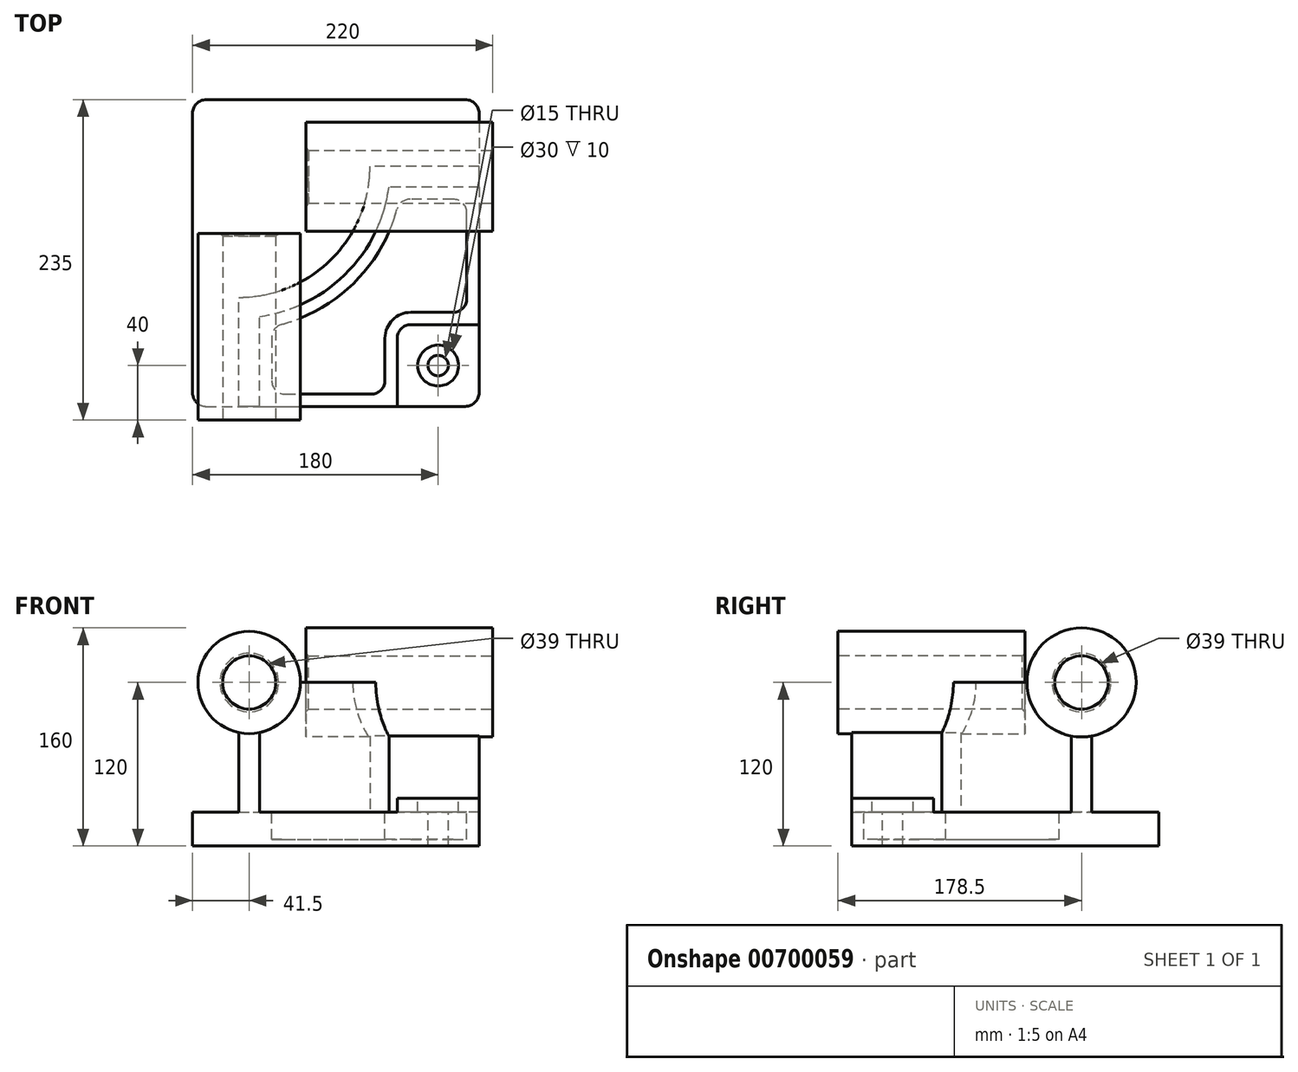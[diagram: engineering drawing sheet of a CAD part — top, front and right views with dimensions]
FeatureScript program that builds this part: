
annotation { "Feature Type Name" : "Feature", "Feature Type Description" : "" }
export const myFeature = defineFeature(function(context is Context, id is Id, definition is map)
    precondition{}
    {
        {
            var Q0;
            Q0=qCreatedBy(makeId("Top.planeOp"),FACE);
            var sketch = newSketch(context, id + "F0", { "sketchPlane" : qUnion([Q0])});
            skLineSegment(sketch, "E0.bottom", {"start": v(-105, 112.5) * mm, "end": v(105, 112.5) * mm});
            skLineSegment(sketch, "E0.top", {"start": v(-105, -112.5) * mm, "end": v(105, -112.5) * mm});
            skLineSegment(sketch, "E0.left", {"start": v(-105, 112.5) * mm, "end": v(-105, -112.5) * mm});
            skLineSegment(sketch, "E0.right", {"start": v(105, 112.5) * mm, "end": v(105, -112.5) * mm});
            skPoint(sketch, "E0.middle", {"position": v(0, 0) * mm});
            skSolve(sketch);
        }
        {
            var Q0;
            Q0=makeQuery(id+"F0.imprint","IMPRINT",FACE,{"disambiguationData":[TD([[makeQuery(id+"F0.imprint","IMPRINT",EDGE,{"derivedFrom":sQuery(id+"F0.wireOp",EDGE,"E0.bottom")}),-1.0]])]});
            extrude(context, id + "F1", {"entities" : qUnion([Q0]), "depth" : 25 * mm, "offsetDistance" : 25 * mm});
        }
        {
            var Q0;
            Q0=makeQuery(id+"F1.opExtrude","CAP_FACE",FACE,{"disambiguationData":[OSD([sQuery(id+"F0.wireOp",EDGE,"E0.bottom"),sQuery(id+"F0.wireOp",EDGE,"E0.top"),sQuery(id+"F0.wireOp",EDGE,"E0.left"),sQuery(id+"F0.wireOp",EDGE,"E0.right")])],"isStart":false});
            var sketch = newSketch(context, id + "F2", { "sketchPlane" : qUnion([Q0])});
            skLineSegment(sketch, "E1", {"start": v(105, 63.5) * mm, "end": v(25, 63.5) * mm});
            skLineSegment(sketch, "E2", {"start": v(-71, -112.5) * mm, "end": v(-71, -32.5) * mm});
            skArc(sketch, "E3", {"start": v(-71, -32.5) * mm, "mid": v(-3.12, -4.38) * mm, "end": v(25, 63.5) * mm});
            skLineSegment(sketch, "E4", {"start": v(-71, 63.5) * mm, "end": v(25, 63.5) * mm, "construction": true});
            skLineSegment(sketch, "E5", {"start": v(-71, 63.5) * mm, "end": v(-71, -32.5) * mm, "construction": true});
            skLineSegment(sketch, "E6.0", {"start": v(105, 48.5) * mm, "end": v(38.98, 48.5) * mm});
            skArc(sketch, "E6.1", {"start": v(-56, -46.48) * mm, "mid": v(7.49, -14.99) * mm, "end": v(38.98, 48.5) * mm});
            skLineSegment(sketch, "E6.2", {"start": v(-56, -112.5) * mm, "end": v(-56, -46.48) * mm});
            skLineSegment(sketch, "E7.0", {"start": v(105, 112.5) * mm, "end": v(105, -112.5) * mm});
            skLineSegment(sketch, "E7.1", {"start": v(-105, -112.5) * mm, "end": v(105, -112.5) * mm});
            skSolve(sketch);
        }
        {
            var Q0;
            {var subQ2=sQuery(id+"F2.wireOp",EDGE,"E1");Q0=makeQuery(id+"F2.imprint","IMPRINT",FACE,{"disambiguationData":[TD([[makeQuery(id+"F2.imprint","IMPRINT",EDGE,{"derivedFrom":subQ2}),1.0]])]});}
            extrude(context, id + "F3", {"entities" : qUnion([Q0]), "operationType" : NewBodyOperationType.ADD, "depth" : 95 * mm, "offsetDistance" : 25 * mm});
        }
        {
            var Q0;
            Q0=makeQuery(id+"F3.boolean.opBoolean","MERGE",FACE,{"derivedFrom":[makeQuery(id+"F1.opExtrude","SWEPT_FACE",FACE,{"disambiguationData":[OSD([sQuery(id+"F0.wireOp",EDGE,"E0.top")])]}),makeQuery(id+"F3.opExtrude","SWEPT_FACE",FACE,{"disambiguationData":[OSD([sQuery(id+"F2.wireOp",EDGE,"E7.1")])]})]});
            var sketch = newSketch(context, id + "F4", { "sketchPlane" : qUnion([Q0])});
            skCircle(sketch, "E8", {"center": v(-63.5, 120) * mm, "radius": 37.5 * mm});
            skSolve(sketch);
        }
        {
            var Q0;
            Q0 = qSketchRegion(id + "F4", true);
            extrude(context, id + "F5", {"entities" : qUnion([Q0]), "operationType" : NewBodyOperationType.ADD, "depth" : 10 * mm, "offsetDistance" : 25 * mm, "hasSecondDirection" : true, "secondDirectionOppositeDirection" : true, "secondDirectionDepth" : (137 - 10) * mm});
        }
        {
            var Q0;
            Q0=makeQuery(id+"F3.boolean.opBoolean","MERGE",FACE,{"derivedFrom":[makeQuery(id+"F1.opExtrude","SWEPT_FACE",FACE,{"disambiguationData":[OSD([sQuery(id+"F0.wireOp",EDGE,"E0.right")])]}),makeQuery(id+"F3.opExtrude","SWEPT_FACE",FACE,{"disambiguationData":[OSD([sQuery(id+"F2.wireOp",EDGE,"E7.0")])]})]});
            var sketch = newSketch(context, id + "F6", { "sketchPlane" : qUnion([Q0])});
            skCircle(sketch, "E9", {"center": v(56, 120) * mm, "radius": 40 * mm});
            skSolve(sketch);
        }
        {
            var Q0;
            Q0 = qSketchRegion(id + "F6", true);
            extrude(context, id + "F7", {"entities" : qUnion([Q0]), "operationType" : NewBodyOperationType.ADD, "depth" : 10 * mm, "offsetDistance" : 25 * mm, "hasSecondDirection" : true, "secondDirectionOppositeDirection" : true, "secondDirectionDepth" : (137 - 10) * mm});
        }
        {
            var Q0;
            {var subQ0=sQuery(id+"F0.wireOp",EDGE,"E0.right");var subQ1=sQuery(id+"F0.wireOp",EDGE,"E0.top");Q0=makeQuery(id+"F3.boolean.opBoolean","SPLIT",FACE,{"disambiguationData":[TD([makeQuery(id+"F3.opExtrude","SWEPT_FACE",FACE,{"disambiguationData":[OSD([sQuery(id+"F2.wireOp",EDGE,"E6.0")])]})])],"derivedFrom":makeQuery(id+"F1.opExtrude","CAP_FACE",FACE,{"disambiguationData":[OSD([sQuery(id+"F0.wireOp",EDGE,"E0.bottom"),subQ1,sQuery(id+"F0.wireOp",EDGE,"E0.left"),subQ0])],"isStart":false})});}
            var sketch = newSketch(context, id + "F8", { "sketchPlane" : qUnion([Q0])});
            skLineSegment(sketch, "E10.bottom", {"start": v(105, -112.5) * mm, "end": v(45, -112.5) * mm});
            skLineSegment(sketch, "E10.top", {"start": v(105, -52.5) * mm, "end": v(45, -52.5) * mm});
            skLineSegment(sketch, "E10.left", {"start": v(105, -112.5) * mm, "end": v(105, -52.5) * mm});
            skLineSegment(sketch, "E10.right", {"start": v(45, -112.5) * mm, "end": v(45, -52.5) * mm});
            skSolve(sketch);
        }
        {
            var Q0;
            Q0 = qSketchRegion(id + "F8", true);
            extrude(context, id + "F9", {"entities" : qUnion([Q0]), "operationType" : NewBodyOperationType.ADD, "depth" : 10 * mm, "offsetDistance" : 25 * mm});
        }
        {
            var Q0;
            Q0=makeQuery(id+"F9.opExtrude","SWEPT_EDGE",EDGE,{"disambiguationData":[OSD([sQuery(id+"F8.wireOp",EDGE,"E10.top"),sQuery(id+"F8.wireOp",EDGE,"E10.right")])]});
            fillet(context, id + "F10", {"entities" : qUnion([Q0]), "radius" : 10 * mm, "tangentPropagation" : true, "allowEdgeOverflow" : false});
        }
        {
            var Q0;
            {var subQ0=sQuery(id+"F0.wireOp",EDGE,"E0.right");var subQ1=sQuery(id+"F0.wireOp",EDGE,"E0.top");Q0=makeQuery(id+"F3.boolean.opBoolean","SPLIT",FACE,{"disambiguationData":[TD([makeQuery(id+"F3.opExtrude","SWEPT_FACE",FACE,{"disambiguationData":[OSD([sQuery(id+"F2.wireOp",EDGE,"E6.0")])]})])],"derivedFrom":makeQuery(id+"F1.opExtrude","CAP_FACE",FACE,{"disambiguationData":[OSD([sQuery(id+"F0.wireOp",EDGE,"E0.bottom"),subQ1,sQuery(id+"F0.wireOp",EDGE,"E0.left"),subQ0])],"isStart":false})});}
            var sketch = newSketch(context, id + "F11", { "sketchPlane" : qUnion([Q0])});
            skLineSegment(sketch, "E11.0", {"start": v(-47, -54.08) * mm, "end": v(-47, -103.5) * mm});
            skArc(sketch, "E11.1", {"start": v(46.58, 39.5) * mm, "mid": v(13.85, -21.35) * mm, "end": v(-47, -54.08) * mm});
            skLineSegment(sketch, "E11.2", {"start": v(-47, -103.5) * mm, "end": v(36, -103.5) * mm});
            skLineSegment(sketch, "E11.3", {"start": v(96, 39.5) * mm, "end": v(46.58, 39.5) * mm});
            skLineSegment(sketch, "E11.4", {"start": v(36, -103.5) * mm, "end": v(36, -62.5) * mm});
            skArc(sketch, "E11.5", {"start": v(36, -62.5) * mm, "mid": v(41.56, -49.06) * mm, "end": v(55, -43.5) * mm});
            skLineSegment(sketch, "E11.6", {"start": v(55, -43.5) * mm, "end": v(96, -43.5) * mm});
            skLineSegment(sketch, "E11.7", {"start": v(96, -43.5) * mm, "end": v(96, 39.5) * mm});
            skSolve(sketch);
        }
        {
            var Q0;
            Q0 = qSketchRegion(id + "F11", true);
            extrude(context, id + "F12", {"entities" : qUnion([Q0]), "operationType" : NewBodyOperationType.REMOVE, "oppositeDirection" : true, "depth" : 20 * mm, "offsetDistance" : 25 * mm});
        }
        {
            var Q0;
            Q0=makeQuery(id+"F9.opExtrude","CAP_FACE",FACE,{"disambiguationData":[OSD([sQuery(id+"F8.wireOp",EDGE,"E10.bottom"),sQuery(id+"F8.wireOp",EDGE,"E10.top"),sQuery(id+"F8.wireOp",EDGE,"E10.left"),sQuery(id+"F8.wireOp",EDGE,"E10.right")])],"isStart":false});
            var sketch = newSketch(context, id + "F13", { "sketchPlane" : qUnion([Q0])});
            skCircle(sketch, "E12", {"center": v(75, -82.5) * mm, "radius": 15 * mm});
            skSolve(sketch);
        }
        {
            var Q0;
            Q0=sQuery(id+"F13.wireOp",VERTEX,"E12.center");
            var Q1;
            Q1=makeQuery(id+"F1.opExtrude","SWEPT_BODY",BODY,{"disambiguationData":[OSD([sQuery(id+"F0.wireOp",EDGE,"E0.bottom"),sQuery(id+"F0.wireOp",EDGE,"E0.top"),sQuery(id+"F0.wireOp",EDGE,"E0.left"),sQuery(id+"F0.wireOp",EDGE,"E0.right")])]});
            hole(context, id + "F14", {"style" : HoleStyle.C_BORE, "endStyle" : HoleEndStyle.THROUGH, "holeDiameter" : 15 * mm, "cBoreDiameter" : 30 * mm, "cBoreDepth" : 10 * mm, "majorDiameter" : 5 * mm, "isTappedThrough" : true, "tappedDepth" : 12 * mm, "tapClearance" : 3, "locations" : qUnion([Q0]), "scope" : qUnion([Q1])});
        }
        {
            var Q0;
            Q0=makeQuery(id+"F12.boolean.opBoolean","COPY",EDGE,{"derivedFrom":makeQuery(id+"F12.opExtrude","SWEPT_EDGE",EDGE,{"disambiguationData":[OSD([sQuery(id+"F11.wireOp",EDGE,"E11.0"),sQuery(id+"F11.wireOp",EDGE,"E11.1")])]})});
            var Q1;
            Q1=makeQuery(id+"F12.boolean.opBoolean","COPY",EDGE,{"derivedFrom":makeQuery(id+"F12.opExtrude","SWEPT_EDGE",EDGE,{"disambiguationData":[OSD([sQuery(id+"F11.wireOp",EDGE,"E11.1"),sQuery(id+"F11.wireOp",EDGE,"E11.3")])]})});
            var Q2;
            Q2=makeQuery(id+"F12.boolean.opBoolean","COPY",EDGE,{"derivedFrom":makeQuery(id+"F12.opExtrude","SWEPT_EDGE",EDGE,{"disambiguationData":[OSD([sQuery(id+"F11.wireOp",EDGE,"E11.3"),sQuery(id+"F11.wireOp",EDGE,"E11.7")])]})});
            var Q3;
            Q3=makeQuery(id+"F12.boolean.opBoolean","COPY",EDGE,{"derivedFrom":makeQuery(id+"F12.opExtrude","SWEPT_EDGE",EDGE,{"disambiguationData":[OSD([sQuery(id+"F11.wireOp",EDGE,"E11.6"),sQuery(id+"F11.wireOp",EDGE,"E11.7")])]})});
            var Q4;
            Q4=makeQuery(id+"F12.boolean.opBoolean","COPY",EDGE,{"derivedFrom":makeQuery(id+"F12.opExtrude","SWEPT_EDGE",EDGE,{"disambiguationData":[OSD([sQuery(id+"F11.wireOp",EDGE,"E11.2"),sQuery(id+"F11.wireOp",EDGE,"E11.4")])]})});
            var Q5;
            Q5=makeQuery(id+"F12.boolean.opBoolean","COPY",EDGE,{"derivedFrom":makeQuery(id+"F12.opExtrude","SWEPT_EDGE",EDGE,{"disambiguationData":[OSD([sQuery(id+"F11.wireOp",EDGE,"E11.0"),sQuery(id+"F11.wireOp",EDGE,"E11.2")])]})});
            fillet(context, id + "F15", {"entities" : qUnion([Q0, Q1, Q2, Q3, Q4, Q5]), "radius" : 10 * mm, "tangentPropagation" : true, "allowEdgeOverflow" : false});
        }
        {
            var Q0;
            Q0=makeQuery(id+"F5.opExtrude","CAP_FACE",FACE,{"disambiguationData":[OSD([sQuery(id+"F4.wireOp",EDGE,"E8")])],"isStart":false});
            var sketch = newSketch(context, id + "F16", { "sketchPlane" : qUnion([Q0])});
            skCircle(sketch, "E13", {"center": v(-63.5, 120) * mm, "radius": 19.5 * mm});
            skSolve(sketch);
        }
        {
            var Q0;
            Q0 = qSketchRegion(id + "F16", true);
            extrude(context, id + "F17", {"entities" : qUnion([Q0]), "operationType" : NewBodyOperationType.REMOVE, "endBound" : BoundingType.THROUGH_ALL, "oppositeDirection" : true, "depth" : 25 * mm, "offsetDistance" : 25 * mm});
        }
        {
            var Q0;
            Q0=makeQuery(id+"F7.opExtrude","CAP_FACE",FACE,{"disambiguationData":[OSD([sQuery(id+"F6.wireOp",EDGE,"E9")])],"isStart":false});
            var sketch = newSketch(context, id + "F18", { "sketchPlane" : qUnion([Q0])});
            skCircle(sketch, "E14", {"center": v(56, 120) * mm, "radius": 19.5 * mm});
            skSolve(sketch);
        }
        {
            var Q0;
            Q0 = qSketchRegion(id + "F18", true);
            extrude(context, id + "F19", {"entities" : qUnion([Q0]), "operationType" : NewBodyOperationType.REMOVE, "endBound" : BoundingType.THROUGH_ALL, "oppositeDirection" : true, "depth" : 25 * mm, "offsetDistance" : 25 * mm});
        }
        {
            var Q0;
            Q0=makeQuery(id+"F17.boolean.opBoolean","COPY",EDGE,{"derivedFrom":makeQuery(id+"F17.opExtrude","CAP_EDGE",EDGE,{"disambiguationData":[OSD([sQuery(id+"F16.wireOp",EDGE,"E13")])],"isStart":true})});
            var Q1;
            Q1=makeQuery(id+"F19.boolean.opBoolean","COPY",EDGE,{"derivedFrom":makeQuery(id+"F19.opExtrude","CAP_EDGE",EDGE,{"disambiguationData":[OSD([sQuery(id+"F18.wireOp",EDGE,"E14")])],"isStart":true})});
            var Q2;
            Q2=makeQuery(id+"F19.boolean.opBoolean","INTERSECT",EDGE,{"derivedFrom":[makeQuery(id+"F7.opExtrude","CAP_FACE",FACE,{"disambiguationData":[OSD([sQuery(id+"F6.wireOp",EDGE,"E9")])],"isStart":true}),makeQuery(id+"F19.opExtrude","SWEPT_FACE",FACE,{"disambiguationData":[OSD([sQuery(id+"F18.wireOp",EDGE,"E14")])]})]});
            var Q3;
            Q3=makeQuery(id+"F17.boolean.opBoolean","INTERSECT",EDGE,{"derivedFrom":[makeQuery(id+"F5.opExtrude","CAP_FACE",FACE,{"disambiguationData":[OSD([sQuery(id+"F4.wireOp",EDGE,"E8")])],"isStart":true}),makeQuery(id+"F17.opExtrude","SWEPT_FACE",FACE,{"disambiguationData":[OSD([sQuery(id+"F16.wireOp",EDGE,"E13")])]})]});
            chamfer(context, id + "F20", {"entities" : qUnion([Q0, Q1, Q2, Q3]), "width" : 2 * mm, "tangentPropagation" : true});
        }
        {
            var Q0;
            Q0=makeQuery(id+"F9.boolean.opBoolean","MERGE",EDGE,{"derivedFrom":[makeQuery(id+"F1.opExtrude","SWEPT_EDGE",EDGE,{"disambiguationData":[OSD([sQuery(id+"F0.wireOp",EDGE,"E0.top"),sQuery(id+"F0.wireOp",EDGE,"E0.right")])]}),makeQuery(id+"F9.opExtrude","SWEPT_EDGE",EDGE,{"disambiguationData":[OSD([sQuery(id+"F8.wireOp",EDGE,"E10.bottom"),sQuery(id+"F8.wireOp",EDGE,"E10.left")])]})]});
            var Q1;
            Q1=makeQuery(id+"F1.opExtrude","SWEPT_EDGE",EDGE,{"disambiguationData":[OSD([sQuery(id+"F0.wireOp",EDGE,"E0.top"),sQuery(id+"F0.wireOp",EDGE,"E0.left")])]});
            var Q2;
            Q2=makeQuery(id+"F1.opExtrude","SWEPT_EDGE",EDGE,{"disambiguationData":[OSD([sQuery(id+"F0.wireOp",EDGE,"E0.bottom"),sQuery(id+"F0.wireOp",EDGE,"E0.left")])]});
            var Q3;
            Q3=makeQuery(id+"F1.opExtrude","SWEPT_EDGE",EDGE,{"disambiguationData":[OSD([sQuery(id+"F0.wireOp",EDGE,"E0.bottom"),sQuery(id+"F0.wireOp",EDGE,"E0.right")])]});
            fillet(context, id + "F21", {"entities" : qUnion([Q0, Q1, Q2, Q3]), "radius" : 10 * mm, "tangentPropagation" : true, "allowEdgeOverflow" : false});
        }
    });
